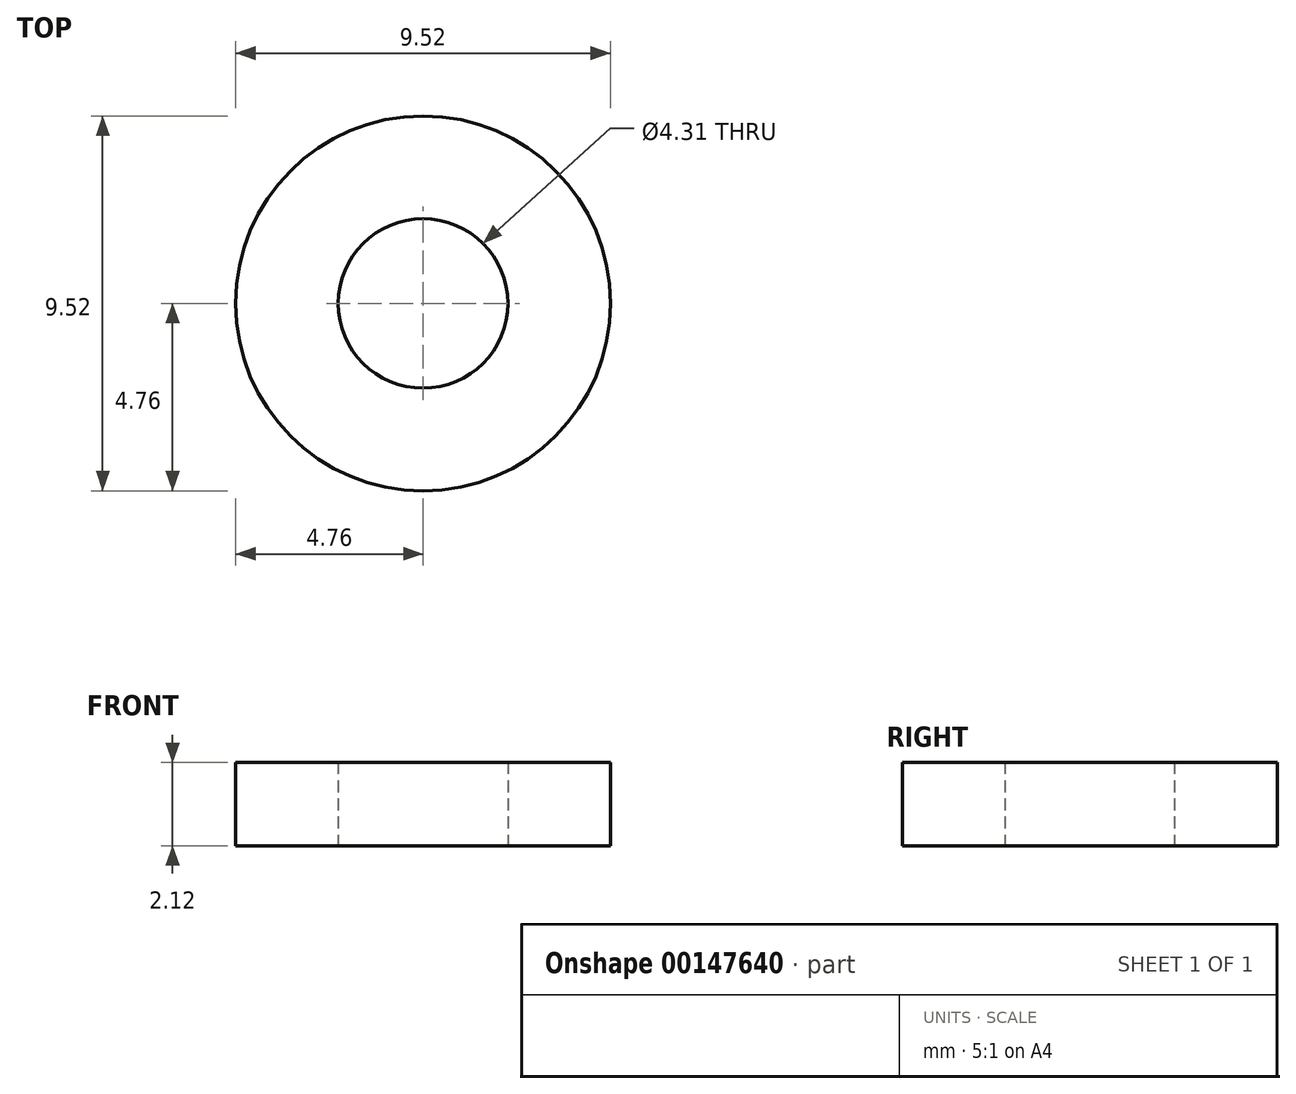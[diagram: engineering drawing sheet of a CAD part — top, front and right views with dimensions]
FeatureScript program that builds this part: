
annotation { "Feature Type Name" : "Feature", "Feature Type Description" : "" }
export const myFeature = defineFeature(function(context is Context, id is Id, definition is map)
    precondition{}
    {
        {
            var Q0;
            Q0=qCreatedBy(makeId("Top.planeOp"),FACE);
            var sketch = newSketch(context, id + "F0", { "sketchPlane" : qUnion([Q0])});
            skCircle(sketch, "E0", {"center": v(0, 0) * mm, "radius": 4.76 * mm});
            skCircle(sketch, "E1", {"center": v(0, 0) * mm, "radius": 2.15 * mm});
            skSolve(sketch);
        }
        {
            var Q0;
            Q0=qSketchRegion(id+"F0",true);
            extrude(context, id + "F1", {"entities" : qUnion([Q0]), "depth" : 2.12 * mm});
        }
    });
